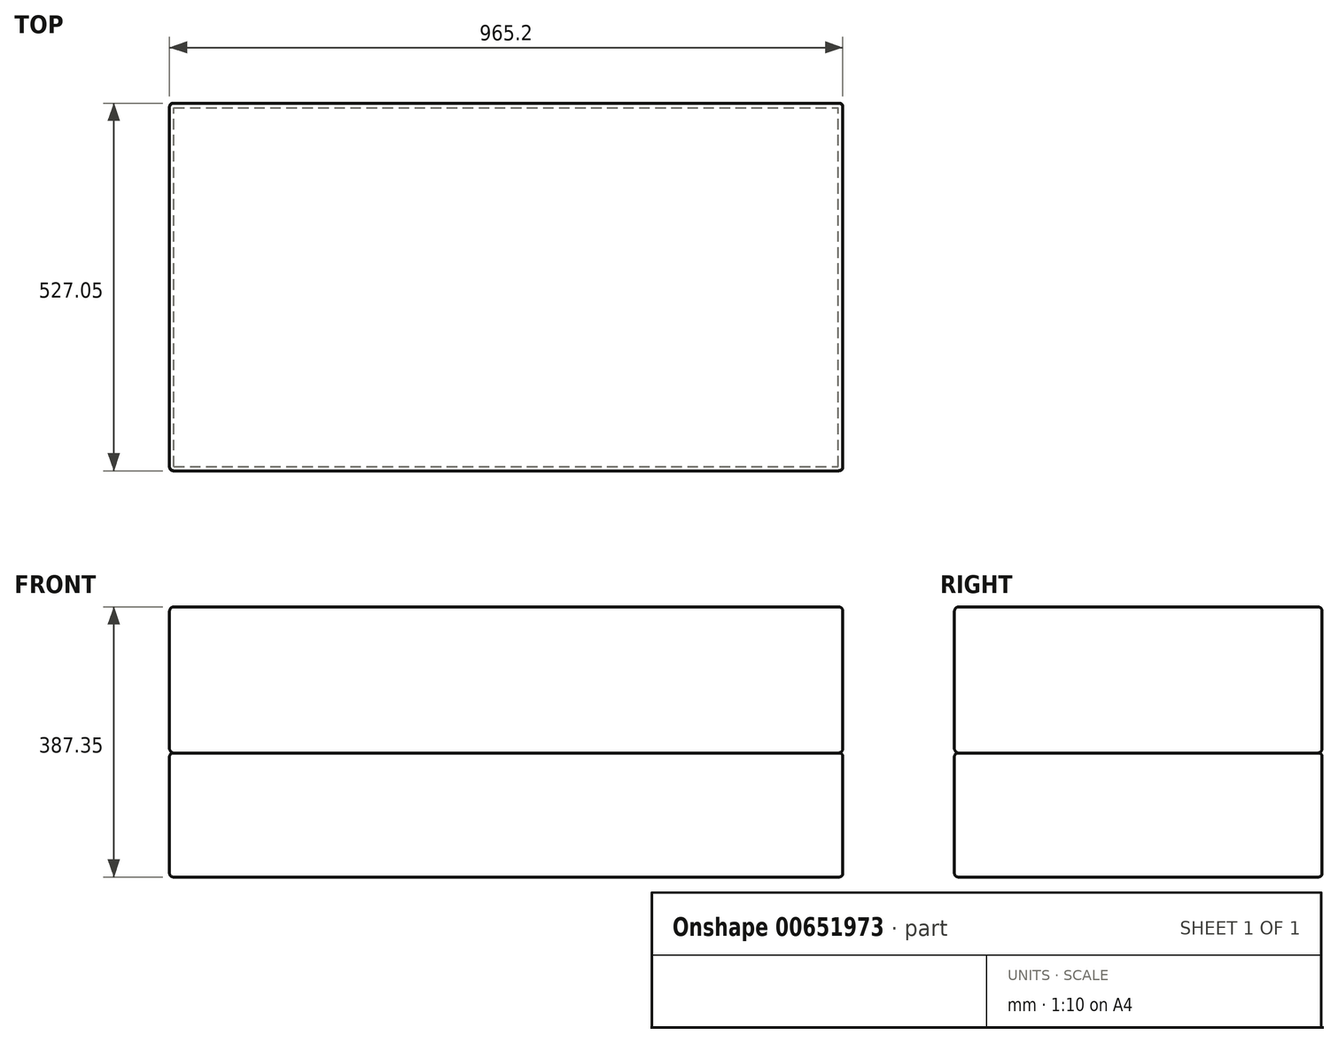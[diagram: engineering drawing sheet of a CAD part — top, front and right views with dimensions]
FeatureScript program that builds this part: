
annotation { "Feature Type Name" : "Feature", "Feature Type Description" : "" }
export const myFeature = defineFeature(function(context is Context, id is Id, definition is map)
    precondition{}
    {
        {
            var Q0;
            Q0=qCreatedBy(makeId("Top.planeOp"),FACE);
            var sketch = newSketch(context, id + "F0", { "sketchPlane" : qUnion([Q0])});
            skLineSegment(sketch, "E0.bottom", {"start": v(0, 0) * mm, "end": v(965.2, 0) * mm});
            skLineSegment(sketch, "E0.top", {"start": v(0, 527.05) * mm, "end": v(965.2, 527.05) * mm});
            skLineSegment(sketch, "E0.left", {"start": v(0, 0) * mm, "end": v(0, 527.05) * mm});
            skLineSegment(sketch, "E0.right", {"start": v(965.2, 0) * mm, "end": v(965.2, 527.05) * mm});
            skSolve(sketch);
        }
        {
            var Q0;
            Q0=makeQuery(id+"F0.imprint","IMPRINT",FACE,{"disambiguationData":[TD([[makeQuery(id+"F0.imprint","IMPRINT",EDGE,{"derivedFrom":sQuery(id+"F0.wireOp",EDGE,"E0.bottom")}),1.0]])]});
            extrude(context, id + "F1", {"entities" : qUnion([Q0]), "depth" : 209.55 * mm, "offsetDistance" : 25.4 * mm});
        }
        {
            var Q0;
            Q0=makeQuery(id+"F1.opExtrude","CAP_EDGE",EDGE,{"disambiguationData":[OSD([sQuery(id+"F0.wireOp",EDGE,"E0.bottom")])],"isStart":true});
            var Q1;
            Q1=makeQuery(id+"F1.opExtrude","CAP_EDGE",EDGE,{"disambiguationData":[OSD([sQuery(id+"F0.wireOp",EDGE,"E0.right")])],"isStart":true});
            var Q2;
            Q2=makeQuery(id+"F1.opExtrude","CAP_EDGE",EDGE,{"disambiguationData":[OSD([sQuery(id+"F0.wireOp",EDGE,"E0.top")])],"isStart":true});
            var Q3;
            Q3=makeQuery(id+"F1.opExtrude","CAP_EDGE",EDGE,{"disambiguationData":[OSD([sQuery(id+"F0.wireOp",EDGE,"E0.left")])],"isStart":true});
            var Q4;
            Q4=makeQuery(id+"F1.opExtrude","CAP_EDGE",EDGE,{"disambiguationData":[OSD([sQuery(id+"F0.wireOp",EDGE,"E0.top")])],"isStart":false});
            var Q5;
            Q5=makeQuery(id+"F1.opExtrude","CAP_EDGE",EDGE,{"disambiguationData":[OSD([sQuery(id+"F0.wireOp",EDGE,"E0.right")])],"isStart":false});
            var Q6;
            Q6=makeQuery(id+"F1.opExtrude","SWEPT_EDGE",EDGE,{"disambiguationData":[OSD([sQuery(id+"F0.wireOp",EDGE,"E0.top"),sQuery(id+"F0.wireOp",EDGE,"E0.right")])]});
            var Q7;
            Q7=makeQuery(id+"F1.opExtrude","SWEPT_EDGE",EDGE,{"disambiguationData":[OSD([sQuery(id+"F0.wireOp",EDGE,"E0.bottom"),sQuery(id+"F0.wireOp",EDGE,"E0.right")])]});
            var Q8;
            Q8=makeQuery(id+"F1.opExtrude","CAP_EDGE",EDGE,{"disambiguationData":[OSD([sQuery(id+"F0.wireOp",EDGE,"E0.bottom")])],"isStart":false});
            var Q9;
            Q9=makeQuery(id+"F1.opExtrude","CAP_EDGE",EDGE,{"disambiguationData":[OSD([sQuery(id+"F0.wireOp",EDGE,"E0.left")])],"isStart":false});
            var Q10;
            Q10=makeQuery(id+"F1.opExtrude","SWEPT_EDGE",EDGE,{"disambiguationData":[OSD([sQuery(id+"F0.wireOp",EDGE,"E0.bottom"),sQuery(id+"F0.wireOp",EDGE,"E0.left")])]});
            var Q11;
            Q11=makeQuery(id+"F1.opExtrude","SWEPT_EDGE",EDGE,{"disambiguationData":[OSD([sQuery(id+"F0.wireOp",EDGE,"E0.top"),sQuery(id+"F0.wireOp",EDGE,"E0.left")])]});
            fillet(context, id + "F2", {"entities" : qUnion([Q0, Q1, Q2, Q3, Q4, Q5, Q6, Q7, Q8, Q9, Q10, Q11]), "radius" : 6.35 * mm, "tangentPropagation" : true, "allowEdgeOverflow" : false});
        }
        {
            var Q0;
            Q0=makeQuery(id+"F1.opExtrude","CAP_FACE",FACE,{"disambiguationData":[OSD([sQuery(id+"F0.wireOp",EDGE,"E0.bottom"),sQuery(id+"F0.wireOp",EDGE,"E0.top"),sQuery(id+"F0.wireOp",EDGE,"E0.left"),sQuery(id+"F0.wireOp",EDGE,"E0.right")])],"isStart":true});
            var sketch = newSketch(context, id + "F3", { "sketchPlane" : qUnion([Q0])});
            skLineSegment(sketch, "E1.0", {"start": v(965.2, -527.05) * mm, "end": v(0, -527.05) * mm});
            skLineSegment(sketch, "E2.0", {"start": v(965.2, 0) * mm, "end": v(965.2, -527.05) * mm});
            skLineSegment(sketch, "E3.0", {"start": v(0, -527.05) * mm, "end": v(0, 0) * mm});
            skLineSegment(sketch, "E4.0", {"start": v(0, 0) * mm, "end": v(965.2, 0) * mm});
            skSolve(sketch);
        }
        {
            var Q0;
            Q0 = qSketchRegion(id + "F3", true);
            extrude(context, id + "F4", {"entities" : qUnion([Q0]), "operationType" : NewBodyOperationType.ADD, "depth" : 177.8 * mm, "offsetDistance" : 25.4 * mm});
        }
        {
            var Q0;
            Q0=makeQuery(id+"F4.opExtrude","CAP_FACE",FACE,{"disambiguationData":[OSD([sQuery(id+"F3.wireOp",EDGE,"E1.0"),sQuery(id+"F3.wireOp",EDGE,"E2.0"),sQuery(id+"F3.wireOp",EDGE,"E3.0"),sQuery(id+"F3.wireOp",EDGE,"E4.0")])],"isStart":false});
            var Q1;
            Q1=makeQuery(id+"F4.opExtrude","SWEPT_FACE",FACE,{"disambiguationData":[OSD([sQuery(id+"F3.wireOp",EDGE,"E4.0")])]});
            var Q2;
            Q2=makeQuery(id+"F4.opExtrude","SWEPT_FACE",FACE,{"disambiguationData":[OSD([sQuery(id+"F3.wireOp",EDGE,"E2.0")])]});
            var Q3;
            Q3=makeQuery(id+"F4.opExtrude","SWEPT_FACE",FACE,{"disambiguationData":[OSD([sQuery(id+"F3.wireOp",EDGE,"E1.0")])]});
            var Q4;
            Q4=makeQuery(id+"F4.opExtrude","SWEPT_FACE",FACE,{"disambiguationData":[OSD([sQuery(id+"F3.wireOp",EDGE,"E3.0")])]});
            fillet(context, id + "F5", {"entities" : qUnion([Q0, Q1, Q2, Q3, Q4]), "radius" : 5.08 * mm, "tangentPropagation" : true, "allowEdgeOverflow" : false});
        }
    });
